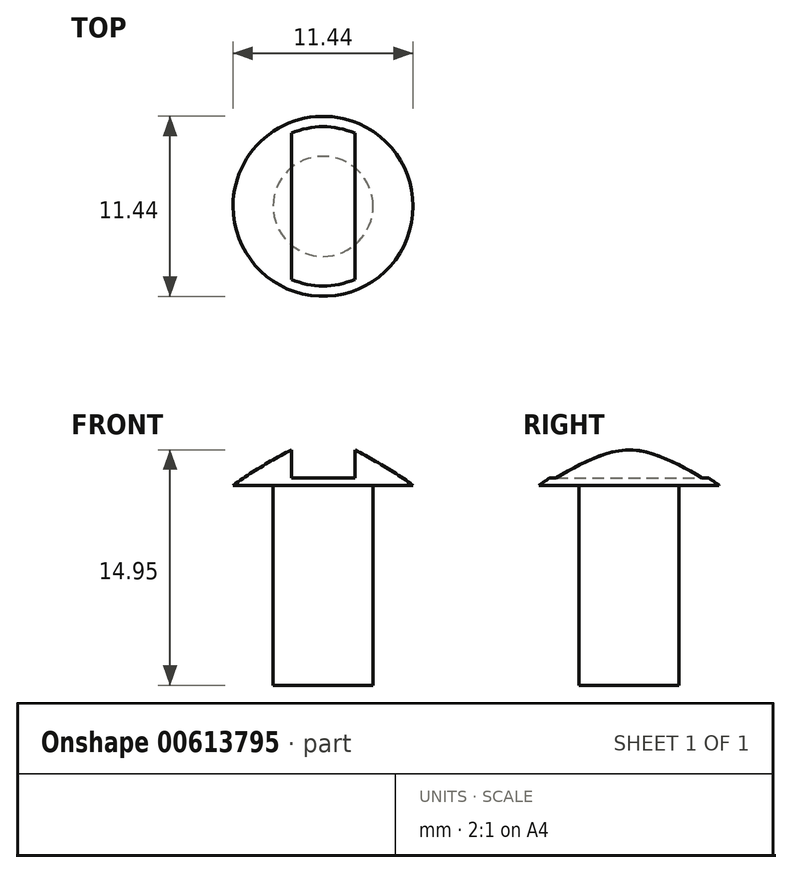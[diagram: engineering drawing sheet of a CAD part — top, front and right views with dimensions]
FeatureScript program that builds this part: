
annotation { "Feature Type Name" : "Feature", "Feature Type Description" : "" }
export const myFeature = defineFeature(function(context is Context, id is Id, definition is map)
    precondition{}
    {
        {
            var Q0;
            Q0=qCreatedBy(makeId("Front.planeOp"),FACE);
            var sketch = newSketch(context, id + "F0", { "sketchPlane" : qUnion([Q0])});
            skLineSegment(sketch, "E0", {"start": v(0, 0) * mm, "end": v(3.17, 0) * mm});
            skLineSegment(sketch, "E1", {"start": v(3.17, 0) * mm, "end": v(3.17, 12.7) * mm});
            skLineSegment(sketch, "E2", {"start": v(5.72, 12.7) * mm, "end": v(3.17, 12.7) * mm});
            skLineSegment(sketch, "E3", {"start": v(0, 0) * mm, "end": v(0, 15.88) * mm});
            skArc(sketch, "E4", {"start": v(5.72, 12.7) * mm, "mid": v(2.95, 14.45) * mm, "end": v(0, 15.88) * mm});
            skSolve(sketch);
        }
        {
            var Q0;
            Q0 = qSketchRegion(id + "F0", true);
            var Q1;
            Q1=sQuery(id+"F0.wireOp",EDGE,"E3");
            revolve(context, id + "F1", {"entities" : qUnion([Q0]), "axis" : qUnion([Q1]), "revolveType" : RevolveType.FULL});
        }
        {
            var Q0;
            Q0=qCreatedBy(makeId("Top.planeOp"),FACE);
            cPlane(context, id + "F2", {"entities" : qUnion([Q0]), "cplaneType" : CPlaneType.OFFSET, "offset" : 16.97 * mm, "width" : 152.4 * mm, "height" : 152.4 * mm});
        }
        {
            var Q0;
            Q0=qCreatedBy(id+"F2.planeOp",FACE);
            var sketch = newSketch(context, id + "F3", { "sketchPlane" : qUnion([Q0])});
            skLineSegment(sketch, "E5", {"start": v(2.02, 0) * mm, "end": v(2.02, 6.25) * mm});
            skLineSegment(sketch, "E6", {"start": v(2.02, 6.25) * mm, "end": v(-2.01, 6.25) * mm});
            skLineSegment(sketch, "E7", {"start": v(-2.01, 6.25) * mm, "end": v(-2.01, -6.75) * mm});
            skLineSegment(sketch, "E8", {"start": v(-2.01, -6.75) * mm, "end": v(2.02, -6.75) * mm});
            skLineSegment(sketch, "E9", {"start": v(2.02, -6.75) * mm, "end": v(2.02, 0) * mm});
            skSolve(sketch);
        }
        {
            var Q0;
            Q0=makeQuery(id+"F3.imprint","IMPRINT",FACE,{"disambiguationData":[TD([[makeQuery(id+"F3.imprint","IMPRINT",EDGE,{"derivedFrom":sQuery(id+"F3.wireOp",EDGE,"E5")}),1.0]])]});
            extrude(context, id + "F4", {"entities" : qUnion([Q0]), "operationType" : NewBodyOperationType.REMOVE, "oppositeDirection" : true, "depth" : 3.8 * mm, "offsetDistance" : 25.4 * mm});
        }
    });
